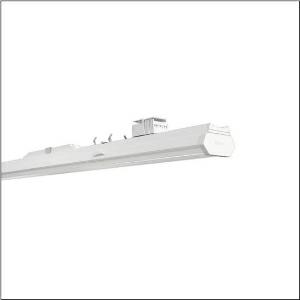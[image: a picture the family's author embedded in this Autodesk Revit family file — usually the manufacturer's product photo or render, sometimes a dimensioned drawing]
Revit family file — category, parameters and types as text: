
# Revit family: licross_r__21_protected_mo_52td127n485g_89bf
name_source: partatom
category: Lighting Fixtures
units: mm (PartAtom-declared; Revit-internal decimal feet)

## family parameters
Cut with Voids When Loaded = No
Host = Face
Light Source = No
Part Type = Normal
Room Calculation Point = No
Round Connector Dimension = Use Diameter
Shared = No

## types (1)
- Licross® 21 Protected MO (1 x LED, 8610 lm, 47.9 W, 4000K)
    Apparent Load = 48 VA
    CIE Flux Codes = 73 92 98 99 100
    Color Rendering = 80
    Color Temperature = 4000K
    Default Elevation = 1800 mm
    Description = Licross® 21 Protected MO, luminaire insert, of sheet steel, galvanised, coil coated, white, length: 1.500mm, width: 90mm, height: 101mm, LED rated luminous flux: 8.610lm, light colour: 840, control gear: ON/OFF, with plug, 3-pole, with phase selection, mains connection: 220..240V, AC, 50/60Hz, rated input power: 48W, halogen-free wiring, primary light control with lens, of plastic, primary optical cover: cover, of PMMA, light emission: direct distribution, primary light characteristic: symmetric, protection rating (complete): IP54, insulation class (complete): insulation class I (protective earthing), certification: CE, ENEC, VDE, UKCA, protection symbol: D if used in an environment with non-conductive dust loads with corresponding accessories, impact resistance: IK06, permissible ambient temperature for indoor applications: -35..+45°C, corresponds to IFS (International Featured Standards) requirements for safety and quality in the food industry, reducing of maximum allowable ambient temperature of 5°C with ceiling mounting, LABS conformity tested according to VDMA 24364:2018-05, packaging unit: 1 piece
    Height = 92 mm
    Lamp = 1 x LED
    Lamp Light Flux = 8610 lm
    Lamp Power = 47.9 W
    Lamp count = 1
    Length = 1500 mm
    Luminous efficacy = 180 lm/W
    Manufacturer = Siteco
    ModVariant = No
    Model = 52TD127N485G
    Mounting Place = Ceiling
    Mounting Type = Pendant
    Number of Poles = 1
    OnlyDefault = Yes
    Power Factor = 1
    Product Name = Licross® 21 Protected MO
    Product group = luminaire insert
    ProductGroupID = 902
    Protection Class = Protection class I
    Protection Degree = IP 54
    RLX_Detail_Level = 1
    RLX_Emergency_Light_Flux = 0 lm
    RLX_Emergency_Type = 0
    RLX_Emergency_Type_DB = No
    RlxData = <blob elided: 20645 chars, md5=42872a91>
    Socket = socket
    Standby Power = 0 W
    System Light Flux = 8610 lm
    System Power = 48 W
    Type Comments = Product without accessories
    Type Image = l_1256148.jpg
    URL = http://relux.com
    VarID = ---
    Voltage = 0 V
    Weight = 0.00 kg
    Width = 88 mm

## geometry (parser evidence)
native form markers: Blend x4, Sweep x12
no freeform markers — native parametric forms only
